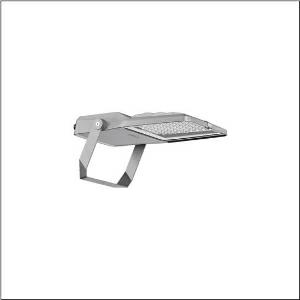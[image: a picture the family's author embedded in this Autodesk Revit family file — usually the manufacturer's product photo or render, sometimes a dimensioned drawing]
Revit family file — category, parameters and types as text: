
# Revit family: floodlight_fl_21_iq_mini___pl43_5xa7772c2a1a_250e
name_source: partatom
category: Lighting Fixtures
units: mm (PartAtom-declared; Revit-internal decimal feet)

## family parameters
Cut with Voids When Loaded = No
Host = Face
Light Source = No
Part Type = Normal
Room Calculation Point = No
Round Connector Dimension = Use Diameter
Shared = No

## types (1)
- --- (1 x LED, 12520 lm, 87.2 W, 3000K)
    Apparent Load = 87 VA
    CIE Flux Codes = 27 78 99 100 100
    Color Rendering = 70
    Color Temperature = 3000K
    Default Elevation = 1800 mm
    Description = Floodlight FL 21 iQ mini, floodlight, primary light control with lens, of PMMA, primary optical cover: protective disc, of toughened safety glass, transparent, light distribution: PL43, light emission: direct distribution, installation type: surface-mounted, LED, High Power LED, rated luminous flux: 12.520lm, luminous efficacy: 144lm/W, light colour: 730, colour temperature: 3000K, control gear: iQ Street-Remote/DALI, control: Street-Remote, Auto-Match, Temp-Guard, Night-Set, Smart-Wire, Desk-Remote (wireless, voltage-free reading and setting of iQ features in the workshop via application-optimized NFC function/RFID function), optimised constant luminous flux control (CLO 2.0), with terminal, 6-pole, mains connection: 220..240V, AC, 50/60Hz, start of lifetime: 87W, end of service life: 92W, reduction: 40W, luminaire housing, of diecast aluminium, powder-coated, Siteco® metallic grey (DB 702S), corrosivity category C5 mid according to DIN EN ISO 12944, suitable for swimming pools, chlorine-resistant, sealing non-destructively replaceable, mounting bracket, of steel, galvanised, powder-coated, Siteco® metallic grey (DB 702S), protection rating (complete): IP66, insulation class (complete): insulation class II (safety insulation), certification: CE, ENEC, VDE, protection symbol: D, impact resistance: IK08, permissible operating ambient temperature: -40..+40°C, permissible operating ambient temperature for outdoor applications: -40..+50°C, standard: DIN EN 12944, LABS conformity tested according to VDMA 24364:2018-05, packaging unit: 1 piece

Light Distribution: PL43
    Height = 70 mm
    Lamp = 1 x LED
    Lamp Light Flux = 12520 lm
    Lamp Power = 87.2 W
    Lamp count = 1
    Length = 485 mm
    Luminous efficacy = 144 lm/W
    Manufacturer = Siteco
    ModVariant = No
    Model = 5XA7772C2A1A
    Number of Poles = 1
    OnlyDefault = Yes
    Power Factor = 1
    Product Name = Floodlight FL 21 iQ mini | PL43
    Product group = floodlight | pylon annexe
    ProductGroupID = 6200
    Protection Class = Protection class II
    Protection Degree = IP 66
    RLX_Detail_Level = 1
    RLX_Emergency_Light_Flux = 0 lm
    RLX_Emergency_Type = 0
    RLX_Emergency_Type_DB = No
    RlxData = <blob elided: 96209 chars, md5=4d44882e>
    Socket = socket
    Standby Power = 0 W
    System Light Flux = 12520 lm
    System Power = 87 W
    Type Comments = factory setting: luminous flux: 100 % | dim-lin: 254 | 456 mA
    Type Image = l_1006845.jpg
    URL = http://relux.com
    VarID = @adj_162574
    Voltage = 0 V
    Weight = 0.00 kg
    Width = 337 mm

## geometry (parser evidence)
native form markers: Blend x4, Sweep x14
no freeform markers — native parametric forms only
